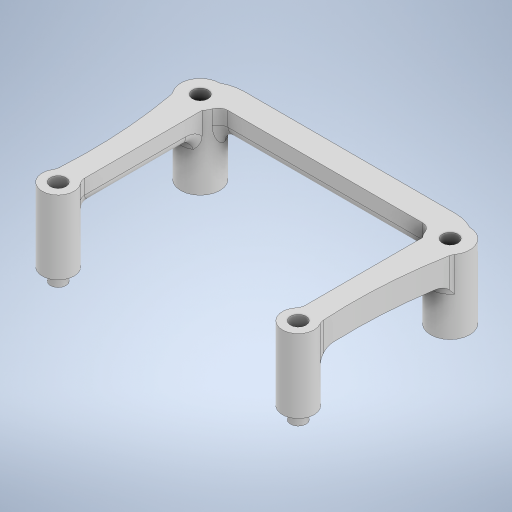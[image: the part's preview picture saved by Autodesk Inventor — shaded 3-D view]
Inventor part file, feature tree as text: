
AUTODESK INVENTOR PART (.ipt)
format: ipt  version: 2024.2 (Build 282272000, 272)  size: 476,160 bytes
history: native  units: mm
features: extrude x5, sketch x5, fillet x1, projected_geometry x1
ambient origin geometry x8: Origin, YZ Plane, XZ Plane, XY Plane, X Axis, Y Axis, Z Axis, Center Point
bodies: Solid1 (feature_tree)
feature tree (12):
  extrude  "Extrusion1"  Depth=5.0mm TaperAngle=0.0deg
  extrude  "Extrusion2"  Depth=5.2mm
  extrude  "Extrusion3"  Depth=8.0mm
  extrude  "Extrusion4"  Depth=49.0mm
  fillet  "Fillet1"  Radius=51.0mm
  extrude  "Extrusion5"  Depth=5.0mm
  sketch  "Sketch2"  dims[d0=6.5mm d1=5.0mm d2=0.0mm]
  sketch  "Sketch3"  dims[d3=6.5mm d4=5.2mm]
  sketch  "Sketch4"  dims[d5=5.2mm d6=8.0mm]
  projected_geometry  "Projected Loop1"
  sketch  "Sketch5"  dims[d7=8.0mm d8=49.0mm d9=51.0mm]
  sketch  "Sketch6"  dims[d11=30.0mm d12=3.2mm d13=3.2mm d14=2.5mm d15=0.0mm d16=3.0mm d17=3.0mm d18=5.0mm d19=0.0mm d21=1.0mm d24=100.0mm d25=100.0mm d26=2.5mm d27=3.0mm d28=3.0mm d29=2.5mm d30=5.0mm d31=0.0mm d32=5.0mm d33=4.0mm d34=4.0mm d35=2.0mm d36=5.0mm d37=0.0mm d38=3.2mm d39=3.2mm d40=3.0mm d41=3.0mm d20=0.5mm]
